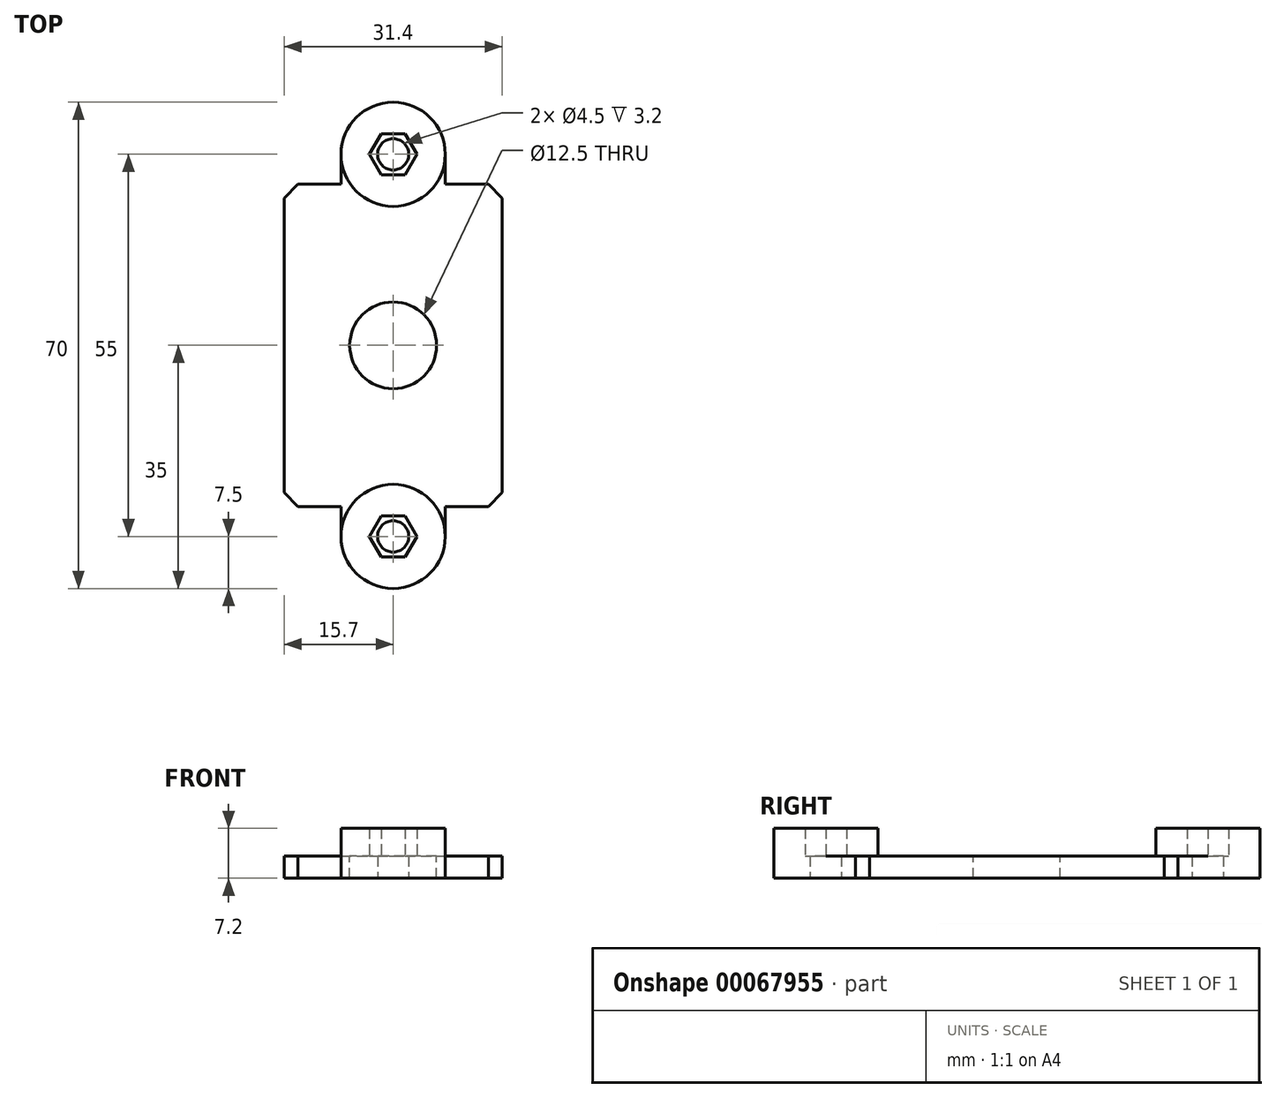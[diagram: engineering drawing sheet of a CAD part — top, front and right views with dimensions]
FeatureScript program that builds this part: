
annotation { "Feature Type Name" : "Feature", "Feature Type Description" : "" }
export const myFeature = defineFeature(function(context is Context, id is Id, definition is map)
    precondition{}
    {
        {
            var Q0;
            Q0=qCreatedBy(makeId("Top.planeOp"),FACE);
            var sketch = newSketch(context, id + "F0", { "sketchPlane" : qUnion([Q0])});
            skLineSegment(sketch, "E0.rect.bottom", {"start": v(12.5, -20) * mm, "end": v(-12.5, -20) * mm});
            skLineSegment(sketch, "E0.rect.top", {"start": v(12.5, 20) * mm, "end": v(-12.5, 20) * mm});
            skLineSegment(sketch, "E0.rect.left", {"start": v(12.5, -20) * mm, "end": v(12.5, 20) * mm});
            skLineSegment(sketch, "E0.rect.right", {"start": v(-12.5, -20) * mm, "end": v(-12.5, 20) * mm});
            skPoint(sketch, "E0.rect.middle", {"position": v(0, 0) * mm});
            skCircle(sketch, "E1", {"center": v(0, 0) * mm, "radius": 6.25 * mm});
            skSolve(sketch);
        }
        {
            var Q0;
            Q0=qSketchRegion(id+"F0",true);
            extrude(context, id + "F1", {"entities" : qUnion([Q0]), "depth" : 3.2 * mm});
        }
        {
            var Q0;
            Q0=makeQuery(id+"F1.opExtrude","CAP_FACE",FACE,{"disambiguationData":[OSD([sQuery(id+"F0.wireOp",EDGE,"E0.rect.bottom"),sQuery(id+"F0.wireOp",EDGE,"E0.rect.top"),sQuery(id+"F0.wireOp",EDGE,"E0.rect.left"),sQuery(id+"F0.wireOp",EDGE,"E0.rect.right"),sQuery(id+"F0.wireOp",EDGE,"E1")])],"isStart":false});
            var sketch = newSketch(context, id + "F2", { "sketchPlane" : qUnion([Q0])});
            skLineSegment(sketch, "E2.rect.bottom", {"start": v(12.5, 20) * mm, "end": v(-12.5, 20) * mm});
            skLineSegment(sketch, "E2.rect.top", {"start": v(12.5, -20) * mm, "end": v(-12.5, -20) * mm});
            skLineSegment(sketch, "E2.rect.left", {"start": v(12.5, 20) * mm, "end": v(12.5, -20) * mm});
            skLineSegment(sketch, "E2.rect.right", {"start": v(-12.5, 20) * mm, "end": v(-12.5, -20) * mm});
            skPoint(sketch, "E2.rect.middle", {"position": v(0, 0) * mm});
            skLineSegment(sketch, "E3.rect.bottom", {"start": v(15.7, 23.2) * mm, "end": v(7.5, 23.2) * mm});
            skLineSegment(sketch, "E3.rect.left", {"start": v(15.7, 23.2) * mm, "end": v(15.7, -23.2) * mm});
            skLineSegment(sketch, "E3.rect.right", {"start": v(-15.7, 23.2) * mm, "end": v(-15.7, -23.2) * mm});
            skLineSegment(sketch, "E4", {"start": v(-7.5, 23.2) * mm, "end": v(-7.5, 27.5) * mm});
            skLineSegment(sketch, "E5", {"start": v(0, 27.5) * mm, "end": v(0, 23.2) * mm, "construction": true});
            skLineSegment(sketch, "E6", {"start": v(0, 0) * mm, "end": v(-6.25, 0) * mm, "construction": true});
            skLineSegment(sketch, "E7.MirrorCS", {"start": v(7.5, 23.2) * mm, "end": v(7.5, 27.5) * mm});
            skArc(sketch, "E8", {"start": v(-7.5, 27.5) * mm, "mid": v(0, 35) * mm, "end": v(7.5, 27.5) * mm});
            skLineSegment(sketch, "E9.MirrorCS", {"start": v(-7.5, -23.2) * mm, "end": v(-7.5, -27.5) * mm});
            skLineSegment(sketch, "E10.MirrorCS", {"start": v(15.7, -23.2) * mm, "end": v(7.5, -23.2) * mm});
            skLineSegment(sketch, "E11.MirrorCS", {"start": v(0, -27.5) * mm, "end": v(0, -23.2) * mm, "construction": true});
            skArc(sketch, "E12.MirrorCS", {"start": v(-7.5, -27.5) * mm, "mid": v(0, -35) * mm, "end": v(7.5, -27.5) * mm});
            skLineSegment(sketch, "E13.MirrorCS", {"start": v(7.5, -23.2) * mm, "end": v(7.5, -27.5) * mm});
            skLineSegment(sketch, "E14.trimOffspring", {"start": v(-7.5, -23.2) * mm, "end": v(-15.7, -23.2) * mm});
            skLineSegment(sketch, "E15.trimOffspring", {"start": v(-7.5, 23.2) * mm, "end": v(-15.7, 23.2) * mm});
            skCircle(sketch, "E16.cCircle", {"center": v(0, 27.5) * mm, "radius": 2.98 * mm, "construction": true});
            skLineSegment(sketch, "E16.0", {"start": v(-1.72, 30.48) * mm, "end": v(1.72, 30.48) * mm});
            skLineSegment(sketch, "E16.1", {"start": v(1.72, 30.48) * mm, "end": v(3.44, 27.5) * mm});
            skLineSegment(sketch, "E16.2", {"start": v(3.44, 27.5) * mm, "end": v(1.72, 24.52) * mm});
            skLineSegment(sketch, "E16.3", {"start": v(1.72, 24.52) * mm, "end": v(-1.72, 24.52) * mm});
            skLineSegment(sketch, "E16.4", {"start": v(-1.72, 24.52) * mm, "end": v(-3.44, 27.5) * mm});
            skLineSegment(sketch, "E16.5", {"start": v(-3.44, 27.5) * mm, "end": v(-1.72, 30.48) * mm});
            skPoint(sketch, "E16.0.midPoint", {"position": v(0, 30.48) * mm});
            skCircle(sketch, "E17.cCircle", {"center": v(0, -27.5) * mm, "radius": 2.98 * mm, "construction": true});
            skLineSegment(sketch, "E17.0", {"start": v(-1.72, -24.52) * mm, "end": v(1.72, -24.52) * mm});
            skLineSegment(sketch, "E17.1", {"start": v(1.72, -24.52) * mm, "end": v(3.44, -27.5) * mm});
            skLineSegment(sketch, "E17.2", {"start": v(3.44, -27.5) * mm, "end": v(1.72, -30.47) * mm});
            skLineSegment(sketch, "E17.3", {"start": v(1.72, -30.48) * mm, "end": v(-1.72, -30.48) * mm});
            skLineSegment(sketch, "E17.4", {"start": v(-1.72, -30.48) * mm, "end": v(-3.44, -27.5) * mm});
            skLineSegment(sketch, "E17.5", {"start": v(-3.44, -27.5) * mm, "end": v(-1.72, -24.52) * mm});
            skPoint(sketch, "E17.0.midPoint", {"position": v(0, -24.52) * mm});
            skSolve(sketch);
        }
        {
            var Q0;
            Q0=qSketchRegion(id+"F2",true);
            extrude(context, id + "F3", {"entities" : qUnion([Q0]), "operationType" : NewBodyOperationType.ADD, "oppositeDirection" : true, "depth" : 40 * mm});
        }
        {
            var Q0;
            Q0=makeQuery(id+"F3.boolean.opBoolean","MERGE",FACE,{"derivedFrom":[makeQuery(id+"F1.opExtrude","CAP_FACE",FACE,{"disambiguationData":[OSD([sQuery(id+"F0.wireOp",EDGE,"E0.rect.bottom"),sQuery(id+"F0.wireOp",EDGE,"E0.rect.top"),sQuery(id+"F0.wireOp",EDGE,"E0.rect.left"),sQuery(id+"F0.wireOp",EDGE,"E0.rect.right"),sQuery(id+"F0.wireOp",EDGE,"E1")])],"isStart":false}),makeQuery(id+"F3.opExtrude","CAP_FACE",FACE,{"disambiguationData":[OSD([sQuery(id+"F2.wireOp",EDGE,"E2.rect.bottom"),sQuery(id+"F2.wireOp",EDGE,"E2.rect.top"),sQuery(id+"F2.wireOp",EDGE,"E2.rect.left"),sQuery(id+"F2.wireOp",EDGE,"E2.rect.right"),sQuery(id+"F2.wireOp",EDGE,"E3.rect.bottom"),sQuery(id+"F2.wireOp",EDGE,"E3.rect.top"),sQuery(id+"F2.wireOp",EDGE,"E3.rect.left"),sQuery(id+"F2.wireOp",EDGE,"E3.rect.right")])],"isStart":true})]});
            var sketch = newSketch(context, id + "F4", { "sketchPlane" : qUnion([Q0])});
            skLineSegment(sketch, "E18", {"start": v(-15.7, 23.2) * mm, "end": v(-30.7, 23.2) * mm});
            skLineSegment(sketch, "E19", {"start": v(-30.7, 23.2) * mm, "end": v(-30.7, -23.2) * mm});
            skLineSegment(sketch, "E20", {"start": v(-30.7, -23.2) * mm, "end": v(-15.7, -23.2) * mm});
            skLineSegment(sketch, "E21", {"start": v(-15.7, -23.2) * mm, "end": v(-15.7, 23.2) * mm});
            skCircle(sketch, "E22", {"center": v(-23.2, 13.2) * mm, "radius": 2.25 * mm});
            skCircle(sketch, "E23", {"center": v(-23.2, -13.2) * mm, "radius": 2.25 * mm});
            skPoint(sketch, "E23.centerSnap0", {"position": v(-23.2, -23.2) * mm});
            skSolve(sketch);
        }
        {
            var Q0;
            Q0=qSketchRegion(id+"F4",true);
            extrude(context, id + "F5", {"entities" : qUnion([Q0]), "operationType" : NewBodyOperationType.ADD, "oppositeDirection" : true, "depth" : 5 * mm});
        }
        {
            var Q0;
            Q0=makeQuery(id+"F3.opExtrude","SWEPT_EDGE",EDGE,{"disambiguationData":[OSD([sQuery(id+"F2.wireOp",EDGE,"E3.rect.bottom"),sQuery(id+"F2.wireOp",EDGE,"E3.rect.left")])]});
            var Q1;
            Q1=makeQuery(id+"F3.opExtrude","SWEPT_EDGE",EDGE,{"disambiguationData":[OSD([sQuery(id+"F2.wireOp",EDGE,"E3.rect.right"),sQuery(id+"F2.wireOp",EDGE,"E15.trimOffspring")])]});
            var Q2;
            Q2=makeQuery(id+"F3.opExtrude","SWEPT_EDGE",EDGE,{"disambiguationData":[OSD([sQuery(id+"F2.wireOp",EDGE,"E3.rect.right"),sQuery(id+"F2.wireOp",EDGE,"E14.trimOffspring")])]});
            var Q3;
            Q3=makeQuery(id+"F3.opExtrude","SWEPT_EDGE",EDGE,{"disambiguationData":[OSD([sQuery(id+"F2.wireOp",EDGE,"E3.rect.bottom"),sQuery(id+"F2.wireOp",EDGE,"E3.rect.left")])]});
            var Q4;
            Q4=makeQuery(id+"F3.opExtrude","SWEPT_EDGE",EDGE,{"disambiguationData":[OSD([sQuery(id+"F2.wireOp",EDGE,"E3.rect.bottom"),sQuery(id+"F2.wireOp",EDGE,"E3.rect.left")])]});
            var Q5;
            Q5=makeQuery(id+"F3.opExtrude","SWEPT_EDGE",EDGE,{"disambiguationData":[OSD([sQuery(id+"F2.wireOp",EDGE,"E3.rect.left"),sQuery(id+"F2.wireOp",EDGE,"E10.MirrorCS")])]});
            var Q6;
            Q6=makeQuery(id+"F3.opExtrude","SWEPT_EDGE",EDGE,{"disambiguationData":[OSD([sQuery(id+"F2.wireOp",EDGE,"E3.rect.right"),sQuery(id+"F2.wireOp",EDGE,"E15.trimOffspring")])]});
            var Q7;
            Q7=makeQuery(id+"F3.opExtrude","SWEPT_EDGE",EDGE,{"disambiguationData":[OSD([sQuery(id+"F2.wireOp",EDGE,"E3.rect.right"),sQuery(id+"F2.wireOp",EDGE,"E14.trimOffspring")])]});
            var Q8;
            Q8=makeQuery(id+"F5.opExtrude","SWEPT_EDGE",EDGE,{"disambiguationData":[OSD([sQuery(id+"F4.wireOp",EDGE,"E18"),sQuery(id+"F4.wireOp",EDGE,"E19")])]});
            var Q9;
            Q9=makeQuery(id+"F5.opExtrude","SWEPT_EDGE",EDGE,{"disambiguationData":[OSD([sQuery(id+"F4.wireOp",EDGE,"E19"),sQuery(id+"F4.wireOp",EDGE,"E20")])]});
            chamfer(context, id + "F6", {"entities" : qUnion([Q0, Q1, Q2, Q3, Q4, Q5, Q6, Q7, Q8, Q9]), "width" : 2 * mm, "tangentPropagation" : true});
        }
        {
            var Q0;
            Q0=makeQuery(id+"F3.opExtrude","CAP_FACE",FACE,{"disambiguationData":[OSD([sQuery(id+"F2.wireOp",EDGE,"E2.rect.bottom"),sQuery(id+"F2.wireOp",EDGE,"E2.rect.top"),sQuery(id+"F2.wireOp",EDGE,"E2.rect.left"),sQuery(id+"F2.wireOp",EDGE,"E2.rect.right"),sQuery(id+"F2.wireOp",EDGE,"E3.rect.bottom"),sQuery(id+"F2.wireOp",EDGE,"E3.rect.left"),sQuery(id+"F2.wireOp",EDGE,"E3.rect.right"),sQuery(id+"F2.wireOp",EDGE,"E4"),sQuery(id+"F2.wireOp",EDGE,"E7.MirrorCS"),sQuery(id+"F2.wireOp",EDGE,"E8"),sQuery(id+"F2.wireOp",EDGE,"E9.MirrorCS"),sQuery(id+"F2.wireOp",EDGE,"E10.MirrorCS"),sQuery(id+"F2.wireOp",EDGE,"E12.MirrorCS"),sQuery(id+"F2.wireOp",EDGE,"E13.MirrorCS"),sQuery(id+"F2.wireOp",EDGE,"E14.trimOffspring"),sQuery(id+"F2.wireOp",EDGE,"E15.trimOffspring"),sQuery(id+"F2.wireOp",EDGE,"E16.0"),sQuery(id+"F2.wireOp",EDGE,"E16.1"),sQuery(id+"F2.wireOp",EDGE,"E16.2"),sQuery(id+"F2.wireOp",EDGE,"E16.3"),sQuery(id+"F2.wireOp",EDGE,"E16.4"),sQuery(id+"F2.wireOp",EDGE,"E16.5"),sQuery(id+"F2.wireOp",EDGE,"E17.0"),sQuery(id+"F2.wireOp",EDGE,"E17.1"),sQuery(id+"F2.wireOp",EDGE,"E17.2"),sQuery(id+"F2.wireOp",EDGE,"E17.3"),sQuery(id+"F2.wireOp",EDGE,"E17.4"),sQuery(id+"F2.wireOp",EDGE,"E17.5")])],"isStart":false});
            var sketch = newSketch(context, id + "F7", { "sketchPlane" : qUnion([Q0])});
            skCircle(sketch, "E24.cCircle", {"center": v(0, 27.5) * mm, "radius": 2.98 * mm, "construction": true});
            skLineSegment(sketch, "E24.0", {"start": v(-1.72, 30.48) * mm, "end": v(1.72, 30.47) * mm});
            skLineSegment(sketch, "E24.1", {"start": v(1.72, 30.47) * mm, "end": v(3.44, 27.5) * mm});
            skLineSegment(sketch, "E24.2", {"start": v(3.44, 27.5) * mm, "end": v(1.72, 24.52) * mm});
            skLineSegment(sketch, "E24.3", {"start": v(1.72, 24.52) * mm, "end": v(-1.72, 24.53) * mm});
            skLineSegment(sketch, "E24.4", {"start": v(-1.72, 24.53) * mm, "end": v(-3.44, 27.5) * mm});
            skLineSegment(sketch, "E24.5", {"start": v(-3.44, 27.5) * mm, "end": v(-1.72, 30.48) * mm});
            skPoint(sketch, "E24.0.midPoint", {"position": v(0, 30.48) * mm});
            skLineSegment(sketch, "E25", {"start": v(0, 0) * mm, "end": v(12.5, 0) * mm, "construction": true});
            skCircle(sketch, "E26", {"center": v(0, 27.5) * mm, "radius": 2.25 * mm});
            skLineSegment(sketch, "E27.MirrorCS", {"start": v(-1.72, -30.48) * mm, "end": v(1.72, -30.47) * mm});
            skCircle(sketch, "E28.MirrorC", {"center": v(0, -27.5) * mm, "radius": 2.98 * mm, "construction": true});
            skLineSegment(sketch, "E29.MirrorCS", {"start": v(1.72, -30.47) * mm, "end": v(3.44, -27.5) * mm});
            skLineSegment(sketch, "E30.MirrorCS", {"start": v(3.44, -27.5) * mm, "end": v(1.72, -24.52) * mm});
            skLineSegment(sketch, "E31.MirrorCS", {"start": v(1.72, -24.52) * mm, "end": v(-1.72, -24.53) * mm});
            skLineSegment(sketch, "E32.MirrorCS", {"start": v(-1.72, -24.53) * mm, "end": v(-3.44, -27.5) * mm});
            skLineSegment(sketch, "E33.MirrorCS", {"start": v(-3.44, -27.5) * mm, "end": v(-1.72, -30.48) * mm});
            skCircle(sketch, "E34.MirrorC", {"center": v(0, -27.5) * mm, "radius": 2.25 * mm});
            skPoint(sketch, "E35.MirrorP", {"position": v(0, -30.48) * mm});
            skSolve(sketch);
        }
        {
            var Q0;
            Q0=qSketchRegion(id+"F7",true);
            extrude(context, id + "F8", {"entities" : qUnion([Q0]), "operationType" : NewBodyOperationType.ADD, "oppositeDirection" : true, "depth" : 3.2 * mm});
        }
        {
            var Q0;
            Q0=makeQuery(id+"F5.boolean.opBoolean","MERGE",FACE,{"derivedFrom":[makeQuery(id+"F3.boolean.opBoolean","MERGE",FACE,{"derivedFrom":[makeQuery(id+"F1.opExtrude","CAP_FACE",FACE,{"disambiguationData":[OSD([sQuery(id+"F0.wireOp",EDGE,"E0.rect.bottom"),sQuery(id+"F0.wireOp",EDGE,"E0.rect.top"),sQuery(id+"F0.wireOp",EDGE,"E0.rect.left"),sQuery(id+"F0.wireOp",EDGE,"E0.rect.right"),sQuery(id+"F0.wireOp",EDGE,"E1")])],"isStart":false}),makeQuery(id+"F3.opExtrude","CAP_FACE",FACE,{"disambiguationData":[OSD([sQuery(id+"F2.wireOp",EDGE,"E2.rect.bottom"),sQuery(id+"F2.wireOp",EDGE,"E2.rect.top"),sQuery(id+"F2.wireOp",EDGE,"E2.rect.left"),sQuery(id+"F2.wireOp",EDGE,"E2.rect.right"),sQuery(id+"F2.wireOp",EDGE,"E3.rect.bottom"),sQuery(id+"F2.wireOp",EDGE,"E3.rect.left"),sQuery(id+"F2.wireOp",EDGE,"E3.rect.right"),sQuery(id+"F2.wireOp",EDGE,"E4"),sQuery(id+"F2.wireOp",EDGE,"E7.MirrorCS"),sQuery(id+"F2.wireOp",EDGE,"E8"),sQuery(id+"F2.wireOp",EDGE,"E9.MirrorCS"),sQuery(id+"F2.wireOp",EDGE,"E10.MirrorCS"),sQuery(id+"F2.wireOp",EDGE,"E12.MirrorCS"),sQuery(id+"F2.wireOp",EDGE,"E13.MirrorCS"),sQuery(id+"F2.wireOp",EDGE,"E14.trimOffspring"),sQuery(id+"F2.wireOp",EDGE,"E15.trimOffspring"),sQuery(id+"F2.wireOp",EDGE,"E16.0"),sQuery(id+"F2.wireOp",EDGE,"E16.1"),sQuery(id+"F2.wireOp",EDGE,"E16.2"),sQuery(id+"F2.wireOp",EDGE,"E16.3"),sQuery(id+"F2.wireOp",EDGE,"E16.4"),sQuery(id+"F2.wireOp",EDGE,"E16.5"),sQuery(id+"F2.wireOp",EDGE,"E17.0"),sQuery(id+"F2.wireOp",EDGE,"E17.1"),sQuery(id+"F2.wireOp",EDGE,"E17.2"),sQuery(id+"F2.wireOp",EDGE,"E17.3"),sQuery(id+"F2.wireOp",EDGE,"E17.4"),sQuery(id+"F2.wireOp",EDGE,"E17.5")])],"isStart":true})]}),makeQuery(id+"F5.opExtrude","CAP_FACE",FACE,{"disambiguationData":[OSD([sQuery(id+"F4.wireOp",EDGE,"E18"),sQuery(id+"F4.wireOp",EDGE,"E19"),sQuery(id+"F4.wireOp",EDGE,"E20"),sQuery(id+"F4.wireOp",EDGE,"E21"),sQuery(id+"F4.wireOp",EDGE,"E22"),sQuery(id+"F4.wireOp",EDGE,"E23")])],"isStart":true})]});
            var sketch = newSketch(context, id + "F9", { "sketchPlane" : qUnion([Q0])});
            skLineSegment(sketch, "E36.rect.bottom", {"start": v(15.7, -35) * mm, "end": v(-30.7, -35) * mm});
            skLineSegment(sketch, "E36.rect.top", {"start": v(15.7, 35) * mm, "end": v(-30.7, 35) * mm});
            skLineSegment(sketch, "E36.rect.left", {"start": v(15.7, -35) * mm, "end": v(15.7, 35) * mm});
            skLineSegment(sketch, "E36.rect.right", {"start": v(-30.7, -35) * mm, "end": v(-30.7, 35) * mm});
            skPoint(sketch, "E36.rect.middle", {"position": v(-7.5, 0) * mm});
            skSolve(sketch);
        }
        {
            var Q0;
            Q0 = qSketchRegion(id + "F9", true);
            extrude(context, id + "F10", {"entities" : qUnion([Q0]), "operationType" : NewBodyOperationType.REMOVE, "oppositeDirection" : true, "depth" : 36.8 * mm});
        }
        {
            var Q0;
            Q0=makeQuery(id+"F10.boolean.opBoolean","MERGE",FACE,{"derivedFrom":[makeQuery(id+"F8.opExtrude","CAP_FACE",FACE,{"disambiguationData":[OSD([sQuery(id+"F7.wireOp",EDGE,"E24.0"),sQuery(id+"F7.wireOp",EDGE,"E24.1"),sQuery(id+"F7.wireOp",EDGE,"E24.2"),sQuery(id+"F7.wireOp",EDGE,"E24.3"),sQuery(id+"F7.wireOp",EDGE,"E24.4"),sQuery(id+"F7.wireOp",EDGE,"E24.5"),sQuery(id+"F7.wireOp",EDGE,"E26")])],"isStart":false}),makeQuery(id+"F8.opExtrude","CAP_FACE",FACE,{"disambiguationData":[OSD([sQuery(id+"F7.wireOp",EDGE,"E27.MirrorCS"),sQuery(id+"F7.wireOp",EDGE,"E29.MirrorCS"),sQuery(id+"F7.wireOp",EDGE,"E30.MirrorCS"),sQuery(id+"F7.wireOp",EDGE,"E31.MirrorCS"),sQuery(id+"F7.wireOp",EDGE,"E32.MirrorCS"),sQuery(id+"F7.wireOp",EDGE,"E33.MirrorCS"),sQuery(id+"F7.wireOp",EDGE,"E34.MirrorC")])],"isStart":false}),makeQuery(id+"F10.opExtrude","CAP_FACE",FACE,{"disambiguationData":[OSD([sQuery(id+"F9.wireOp",EDGE,"E36.rect.bottom"),sQuery(id+"F9.wireOp",EDGE,"E36.rect.top"),sQuery(id+"F9.wireOp",EDGE,"E36.rect.left"),sQuery(id+"F9.wireOp",EDGE,"E36.rect.right")])],"isStart":false})]});
            var sketch = newSketch(context, id + "F11", { "sketchPlane" : qUnion([Q0])});
            skLineSegment(sketch, "E37.rect.bottom", {"start": v(12.5, 20) * mm, "end": v(-12.5, 20) * mm});
            skLineSegment(sketch, "E37.rect.top", {"start": v(12.5, -20) * mm, "end": v(-12.5, -20) * mm});
            skLineSegment(sketch, "E37.rect.left", {"start": v(12.5, 20) * mm, "end": v(12.5, -20) * mm});
            skLineSegment(sketch, "E37.rect.right", {"start": v(-12.5, 20) * mm, "end": v(-12.5, -20) * mm});
            skPoint(sketch, "E37.rect.middle", {"position": v(0, 0) * mm});
            skCircle(sketch, "E38", {"center": v(0, 0) * mm, "radius": 6.25 * mm});
            skSolve(sketch);
        }
        {
            var Q0;
            Q0 = qSketchRegion(id + "F11", true);
            extrude(context, id + "F12", {"entities" : qUnion([Q0]), "operationType" : NewBodyOperationType.ADD, "oppositeDirection" : true, "depth" : 3.2 * mm});
        }
        {
            var Q0;
            Q0=makeQuery(id+"F12.boolean.opBoolean","MERGE",FACE,{"derivedFrom":[makeQuery(id+"F10.boolean.opBoolean","MERGE",FACE,{"derivedFrom":[makeQuery(id+"F8.opExtrude","CAP_FACE",FACE,{"disambiguationData":[OSD([sQuery(id+"F7.wireOp",EDGE,"E24.0"),sQuery(id+"F7.wireOp",EDGE,"E24.1"),sQuery(id+"F7.wireOp",EDGE,"E24.2"),sQuery(id+"F7.wireOp",EDGE,"E24.3"),sQuery(id+"F7.wireOp",EDGE,"E24.4"),sQuery(id+"F7.wireOp",EDGE,"E24.5"),sQuery(id+"F7.wireOp",EDGE,"E26")])],"isStart":false}),makeQuery(id+"F8.opExtrude","CAP_FACE",FACE,{"disambiguationData":[OSD([sQuery(id+"F7.wireOp",EDGE,"E27.MirrorCS"),sQuery(id+"F7.wireOp",EDGE,"E29.MirrorCS"),sQuery(id+"F7.wireOp",EDGE,"E30.MirrorCS"),sQuery(id+"F7.wireOp",EDGE,"E31.MirrorCS"),sQuery(id+"F7.wireOp",EDGE,"E32.MirrorCS"),sQuery(id+"F7.wireOp",EDGE,"E33.MirrorCS"),sQuery(id+"F7.wireOp",EDGE,"E34.MirrorC")])],"isStart":false}),makeQuery(id+"F10.opExtrude","CAP_FACE",FACE,{"disambiguationData":[OSD([sQuery(id+"F9.wireOp",EDGE,"E36.rect.bottom"),sQuery(id+"F9.wireOp",EDGE,"E36.rect.top"),sQuery(id+"F9.wireOp",EDGE,"E36.rect.left"),sQuery(id+"F9.wireOp",EDGE,"E36.rect.right")])],"isStart":false})]}),makeQuery(id+"F12.opExtrude","CAP_FACE",FACE,{"disambiguationData":[OSD([sQuery(id+"F11.wireOp",EDGE,"E37.rect.bottom"),sQuery(id+"F11.wireOp",EDGE,"E37.rect.top"),sQuery(id+"F11.wireOp",EDGE,"E37.rect.left"),sQuery(id+"F11.wireOp",EDGE,"E37.rect.right"),sQuery(id+"F11.wireOp",EDGE,"e01bcde1-b1cc-4272-b2a3-0804ea6b9ef7"),sQuery(id+"F11.wireOp",EDGE,"E38")])],"isStart":true})]});
            var sketch = newSketch(context, id + "F13", { "sketchPlane" : qUnion([Q0])});
            skCircle(sketch, "E39.cCircle", {"center": v(0, 27.5) * mm, "radius": 2.98 * mm, "construction": true});
            skLineSegment(sketch, "E39.0", {"start": v(-1.72, 30.48) * mm, "end": v(1.72, 30.48) * mm});
            skLineSegment(sketch, "E39.1", {"start": v(1.72, 30.48) * mm, "end": v(3.44, 27.5) * mm});
            skLineSegment(sketch, "E39.2", {"start": v(3.44, 27.5) * mm, "end": v(1.72, 24.53) * mm});
            skLineSegment(sketch, "E39.3", {"start": v(1.72, 24.52) * mm, "end": v(-1.72, 24.52) * mm});
            skLineSegment(sketch, "E39.4", {"start": v(-1.72, 24.52) * mm, "end": v(-3.44, 27.5) * mm});
            skLineSegment(sketch, "E39.5", {"start": v(-3.44, 27.5) * mm, "end": v(-1.72, 30.47) * mm});
            skPoint(sketch, "E39.0.midPoint", {"position": v(0, 30.48) * mm});
            skCircle(sketch, "E40.cCircle", {"center": v(0, -27.5) * mm, "radius": 2.98 * mm, "construction": true});
            skLineSegment(sketch, "E40.0", {"start": v(-1.72, -24.52) * mm, "end": v(1.72, -24.52) * mm});
            skLineSegment(sketch, "E40.1", {"start": v(1.72, -24.53) * mm, "end": v(3.44, -27.5) * mm});
            skLineSegment(sketch, "E40.2", {"start": v(3.44, -27.5) * mm, "end": v(1.72, -30.47) * mm});
            skLineSegment(sketch, "E40.3", {"start": v(1.72, -30.48) * mm, "end": v(-1.72, -30.48) * mm});
            skLineSegment(sketch, "E40.4", {"start": v(-1.72, -30.48) * mm, "end": v(-3.44, -27.5) * mm});
            skLineSegment(sketch, "E40.5", {"start": v(-3.44, -27.5) * mm, "end": v(-1.72, -24.52) * mm});
            skPoint(sketch, "E40.0.midPoint", {"position": v(0, -24.52) * mm});
            skCircle(sketch, "E41", {"center": v(0, 27.5) * mm, "radius": 7.5 * mm});
            skCircle(sketch, "E42", {"center": v(0, -27.5) * mm, "radius": 7.5 * mm});
            skSolve(sketch);
        }
        {
            var Q0;
            Q0 = qSketchRegion(id + "F13", true);
            extrude(context, id + "F14", {"entities" : qUnion([Q0]), "operationType" : NewBodyOperationType.ADD, "depth" : 4 * mm});
        }
    });
